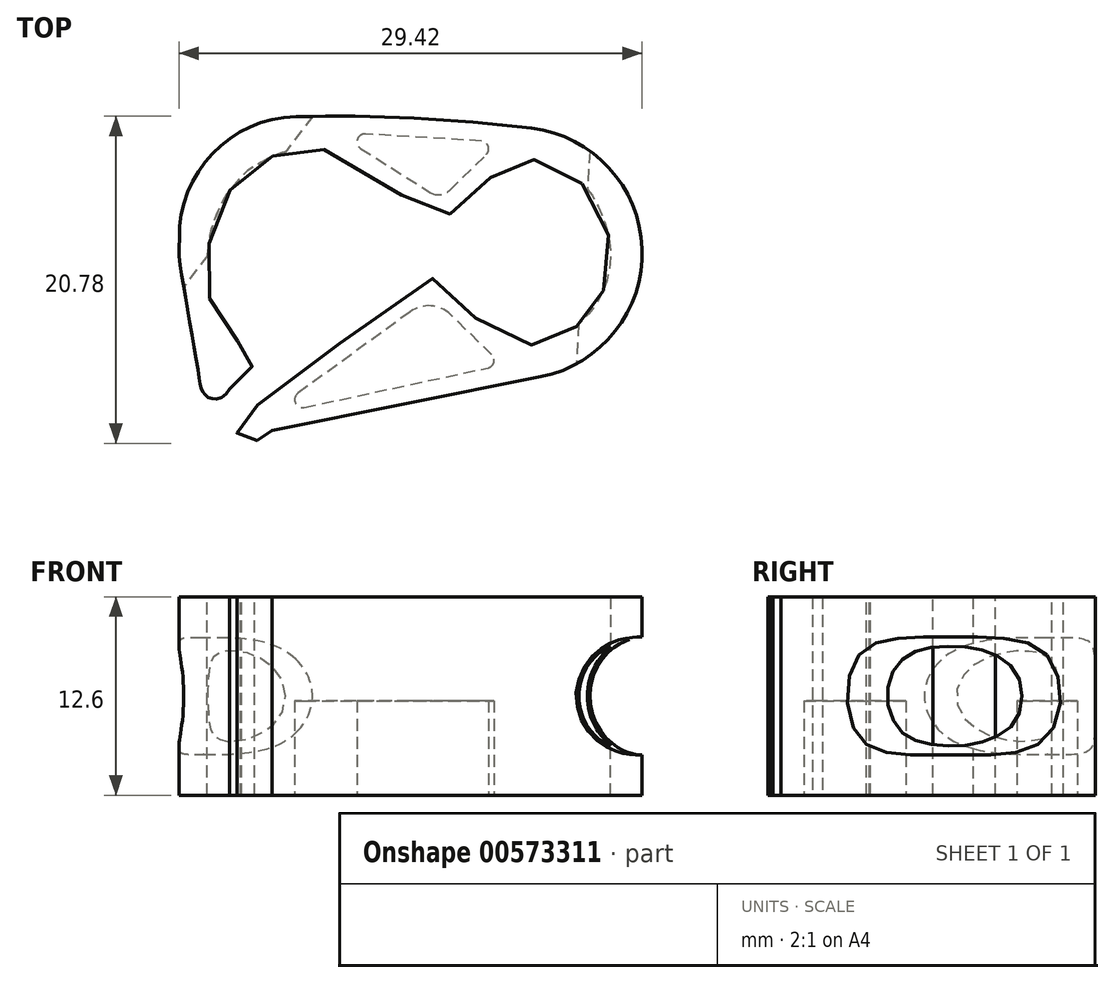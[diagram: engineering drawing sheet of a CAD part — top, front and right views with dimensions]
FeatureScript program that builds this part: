
annotation { "Feature Type Name" : "Feature", "Feature Type Description" : "" }
export const myFeature = defineFeature(function(context is Context, id is Id, definition is map)
    precondition{}
    {
        {
            var Q0;
            Q0=qCreatedBy(makeId("Top.planeOp"),FACE);
            var sketch = newSketch(context, id + "F0", { "sketchPlane" : qUnion([Q0])});
            skArc(sketch, "E0", {"start": v(11.96, -7.07) * mm, "mid": v(18.39, 1.08) * mm, "end": v(11.37, 8.72) * mm});
            skArc(sketch, "E1", {"start": v(-3.59, 9.45) * mm, "mid": v(-8.9, 7.12) * mm, "end": v(-11, 1.72) * mm});
            skArc(sketch, "E2", {"start": v(11.37, 8.72) * mm, "mid": v(3.9, 9.36) * mm, "end": v(-3.59, 9.45) * mm});
            skFitSpline(sketch, "E3", {"points": [v(-11, 1.72) * mm, v(-11, 0.44) * mm, v(-10.77, -1.18) * mm, v(-10.33, -3.66) * mm, v(-9.9, -6.13) * mm, v(-9.7, -7.38) * mm, v(-9.65, -7.7) * mm, v(-9.58, -7.94) * mm, v(-9.42, -8.15) * mm, v(-9.23, -8.35) * mm, v(-8.96, -8.46) * mm, v(-8.63, -8.5) * mm, v(-8.18, -8.3) * mm, v(-7.82, -7.86) * mm], "startDerivative": vector(-0.62, -12.7) * mm, "endDerivative": vector(4.68, 7.47) * mm});
            skLineSegment(sketch, "E4", {"start": v(11.96, -7.07) * mm, "end": v(-5.1, -10.48) * mm});
            skFitSpline(sketch, "E5", {"points": [v(-5.1, -10.48) * mm, v(-5.45, -10.95) * mm, v(-5.51, -11.02) * mm, v(-5.58, -11.03) * mm, v(-5.67, -11.01) * mm, v(-5.74, -11) * mm, v(-5.77, -10.98) * mm, v(-5.82, -11.05) * mm, v(-5.85, -11.1) * mm, v(-5.93, -11.15) * mm, v(-6.02, -11.14) * mm, v(-6.05, -11.12) * mm, v(-6.75, -11.28) * mm, v(-6.96, -11.3) * mm, v(-7.08, -11.26) * mm, v(-7.18, -11.17) * mm, v(-7.26, -11.04) * mm, v(-7.32, -10.93) * mm, v(-7.34, -10.79) * mm, v(-7.35, -10.64) * mm, v(-7.29, -10.48) * mm, v(-7.06, -10.26) * mm, v(-7.1, -10.05) * mm, v(-6.87, -9.77) * mm, v(-6.31, -9.21) * mm, v(-5.88, -8.63) * mm, v(-5.4, -8.14) * mm, v(-4.72, -7.68) * mm, v(4.34, -1.18) * mm, v(4.58, -0.98) * mm, v(4.82, -0.86) * mm, v(5.17, -0.83) * mm, v(5.56, -0.98) * mm, v(5.9, -1.3) * mm, v(6.49, -1.93) * mm, v(8.7, -4.2) * mm, v(9.71, -4.74) * mm, v(10.67, -4.97) * mm, v(11.62, -5.03) * mm, v(12.34, -4.91) * mm, v(13.23, -4.62) * mm, v(14.01, -4.1) * mm, v(14.42, -3.67) * mm, v(14.94, -3.13) * mm, v(15.4, -2.55) * mm, v(15.72, -2.02) * mm, v(16.03, -1.33) * mm, v(16.3, -0.28) * mm, v(16.38, 0.68) * mm, v(16.27, 1.83) * mm, v(15.86, 3.13) * mm, v(15.34, 4.24) * mm, v(14.78, 4.98) * mm, v(14, 5.72) * mm, v(13.41, 6.17) * mm, v(12.37, 6.61) * mm, v(11.34, 6.72) * mm, v(10.74, 6.69) * mm, v(10, 6.46) * mm, v(9.56, 6.24) * mm, v(8.52, 5.39) * mm, v(7.48, 4.54) * mm, v(6.74, 3.8) * mm, v(6.33, 3.35) * mm, v(5.89, 3.2) * mm, v(5.4, 3.17) * mm, v(4.52, 3.65) * mm, v(3.48, 4.24) * mm, v(-0.52, 6.9) * mm, v(-1.37, 7.2) * mm, v(-2, 7.43) * mm, v(-2.82, 7.43) * mm, v(-3.9, 7.28) * mm, v(-4.82, 7.06) * mm, v(-5.7, 6.61) * mm, v(-6.71, 5.98) * mm, v(-7.3, 5.35) * mm, v(-7.93, 4.61) * mm, v(-8.38, 3.8) * mm, v(-8.82, 2.76) * mm, v(-9.12, 1.42) * mm, v(-9.23, 0) * mm, v(-9.2, -0.5) * mm, v(-9.12, -1.62) * mm, v(-8.97, -2.36) * mm, v(-8.04, -3.17) * mm, v(-7.64, -3.62) * mm, v(-7.34, -4.7) * mm, v(-7.2, -4.88) * mm, v(-6.6, -4.8) * mm, v(-6.3, -5.1) * mm, v(-6.23, -5.73) * mm, v(-6.3, -6.28) * mm, v(-6.67, -6.73) * mm, v(-6.97, -7.17) * mm, v(-7.3, -7.36) * mm, v(-7.66, -7.5) * mm, v(-7.82, -7.6) * mm, v(-7.82, -7.86) * mm, v(-7.93, -8.02) * mm], "startDerivative": vector(-44.55, -59.06) * mm, "endDerivative": vector(-25.38, -25.79) * mm});
            skSolve(sketch);
        }
        {
            var Q0;
            Q0=makeQuery(id+"F0.imprint","IMPRINT",FACE,{"disambiguationData":[TD([[makeQuery(id+"F0.imprint","IMPRINT",EDGE,{"derivedFrom":sQuery(id+"F0.wireOp",EDGE,"E0")}),1.0]])]});
            extrude(context, id + "F1", {"entities" : qUnion([Q0]), "depth" : 12.6 * mm, "offsetDistance" : 25 * mm});
        }
        {
            var Q0;
            Q0=qCreatedBy(makeId("Top.planeOp"),FACE);
            var sketch = newSketch(context, id + "F2", { "sketchPlane" : qUnion([Q0])});
            skLineSegment(sketch, "E6", {"start": v(8.18, 7.9) * mm, "end": v(0.8, 8.35) * mm});
            skLineSegment(sketch, "E7", {"start": v(0.5, 7.43) * mm, "end": v(4.92, 4.64) * mm});
            skLineSegment(sketch, "E8", {"start": v(6.15, 4.77) * mm, "end": v(8.5, 7.05) * mm});
            skPoint(sketch, "E9.visualSharp", {"position": v(-1.13, 8.47) * mm});
            skArc(sketch, "E9.filletArc", {"start": v(0.8, 8.35) * mm, "mid": v(0.3, 8) * mm, "end": v(0.5, 7.43) * mm});
            skPoint(sketch, "E10.visualSharp", {"position": v(9.3, 7.84) * mm});
            skArc(sketch, "E10.filletArc", {"start": v(8.5, 7.05) * mm, "mid": v(8.62, 7.58) * mm, "end": v(8.18, 7.9) * mm});
            skPoint(sketch, "E11.visualSharp", {"position": v(5.59, 4.22) * mm});
            skArc(sketch, "E11.filletArc", {"start": v(4.92, 4.64) * mm, "mid": v(5.56, 4.5) * mm, "end": v(6.15, 4.77) * mm});
            skLineSegment(sketch, "E12", {"start": v(3.66, -2.94) * mm, "end": v(-3.47, -8.12) * mm});
            skLineSegment(sketch, "E13", {"start": v(-3.07, -9.01) * mm, "end": v(8.6, -6.5) * mm});
            skLineSegment(sketch, "E14", {"start": v(8.84, -5.66) * mm, "end": v(6.23, -3.12) * mm});
            skArc(sketch, "E15.filletArc", {"start": v(-3.47, -8.12) * mm, "mid": v(-3.64, -8.73) * mm, "end": v(-3.07, -9.01) * mm});
            skPoint(sketch, "E16.visualSharp", {"position": v(5.02, -1.95) * mm});
            skArc(sketch, "E16.filletArc", {"start": v(6.23, -3.12) * mm, "mid": v(4.98, -2.56) * mm, "end": v(3.66, -2.94) * mm});
            skPoint(sketch, "E17.visualSharp", {"position": v(9.5, -6.3) * mm});
            skArc(sketch, "E17.filletArc", {"start": v(8.6, -6.5) * mm, "mid": v(8.97, -6.16) * mm, "end": v(8.84, -5.66) * mm});
            skSolve(sketch);
        }
        {
            var Q0;
            Q0=makeQuery(id+"F2.imprint","IMPRINT",FACE,{"disambiguationData":[TD([[makeQuery(id+"F2.imprint","IMPRINT",EDGE,{"derivedFrom":sQuery(id+"F2.wireOp",EDGE,"E6")}),1.0]])]});
            var Q1;
            Q1=makeQuery(id+"F2.imprint","IMPRINT",FACE,{"disambiguationData":[TD([[makeQuery(id+"F2.imprint","IMPRINT",EDGE,{"derivedFrom":sQuery(id+"F2.wireOp",EDGE,"E12")}),1.0]])]});
            extrude(context, id + "F3", {"entities" : qUnion([Q0, Q1]), "operationType" : NewBodyOperationType.REMOVE, "depth" : 6 * mm, "offsetDistance" : 25 * mm});
        }
        {
            var Q0;
            Q0=makeQuery(id+"F1.opExtrude","CAP_FACE",FACE,{"disambiguationData":[OSD([sQuery(id+"F0.wireOp",EDGE,"E0"),sQuery(id+"F0.wireOp",EDGE,"E1"),sQuery(id+"F0.wireOp",EDGE,"E2"),sQuery(id+"F0.wireOp",EDGE,"E3"),sQuery(id+"F0.wireOp",EDGE,"E4"),sQuery(id+"F0.wireOp",EDGE,"E5")])],"isStart":false});
            var Q1;
            Q1=makeQuery(id+"F1.opExtrude","CAP_FACE",FACE,{"disambiguationData":[OSD([sQuery(id+"F0.wireOp",EDGE,"E0"),sQuery(id+"F0.wireOp",EDGE,"E1"),sQuery(id+"F0.wireOp",EDGE,"E2"),sQuery(id+"F0.wireOp",EDGE,"E3"),sQuery(id+"F0.wireOp",EDGE,"E4"),sQuery(id+"F0.wireOp",EDGE,"E5")])],"isStart":true});
            cPlane(context, id + "F4", {"entities" : qUnion([Q0, Q1]), "cplaneType" : CPlaneType.MID_PLANE, "offset" : 25 * mm, "width" : 150 * mm, "height" : 150 * mm});
        }
        {
            var Q0;
            Q0=makeQuery(id+"F1.opExtrude","SWEPT_EDGE",EDGE,{"disambiguationData":[OSD([sQuery(id+"F0.wireOp",EDGE,"E4"),sQuery(id+"F0.wireOp",EDGE,"E5")])]});
            cPlane(context, id + "F5", {"entities" : qUnion([Q0]), "cplaneType" : CPlaneType.LINE_ANGLE, "offset" : 25 * mm, "angle" : 53 * degree, "oppositeDirection" : true, "width" : 150 * mm, "height" : 150 * mm});
        }
        {
            var Q0;
            Q0=qCreatedBy(id+"F5.planeOp",FACE);
            var sketch = newSketch(context, id + "F6", { "sketchPlane" : qUnion([Q0])});
            skLineSegment(sketch, "E18.0.0", {"start": v(2.23, 0) * mm, "end": v(13.8, 0) * mm});
            skLineSegment(sketch, "E18.0.1", {"start": v(13.8, 0) * mm, "end": v(13.8, 12.6) * mm});
            skLineSegment(sketch, "E18.0.2", {"start": v(13.8, 12.6) * mm, "end": v(2.23, 12.6) * mm});
            skLineSegment(sketch, "E18.0.3", {"start": v(2.23, 12.6) * mm, "end": v(2.23, 0) * mm});
            skCircle(sketch, "E19", {"center": v(-11.44, 6.3) * mm, "radius": 3.7 * mm});
            skPoint(sketch, "E20", {"position": v(2.23, 6.3) * mm});
            skLineSegment(sketch, "E21", {"start": v(-11.44, 2.6) * mm, "end": v(-11.44, 10) * mm});
            skPoint(sketch, "E22.orphan", {"position": v(-11.44, 12.6) * mm});
            skPoint(sketch, "E23.orphan", {"position": v(-11.44, 0) * mm});
            skSolve(sketch);
        }
        {
            var Q0;
            {var subQ0=sQuery(id+"F6.wireOp",EDGE,"E21");Q0=makeQuery(id+"F6.imprint","IMPRINT",FACE,{"disambiguationData":[TD([[makeQuery(id+"F6.imprint","IMPRINT",EDGE,{"derivedFrom":subQ0}),1.0]])]});}
            var Q1;
            {var subQ0=sQuery(id+"F6.wireOp",EDGE,"E21");Q1=makeQuery(id+"F6.imprint","IMPRINT",FACE,{"disambiguationData":[TD([[makeQuery(id+"F6.imprint","IMPRINT",EDGE,{"derivedFrom":subQ0}),-1.0]])]});}
            extrude(context, id + "F7", {"entities" : qUnion([Q0, Q1]), "operationType" : NewBodyOperationType.REMOVE, "endBound" : BoundingType.THROUGH_ALL, "oppositeDirection" : true, "depth" : 25 * mm, "offsetDistance" : 25 * mm});
        }
        {
            var Q0;
            Q0=makeQuery(id+"F1.opExtrude","SWEPT_EDGE",EDGE,{"disambiguationData":[OSD([sQuery(id+"F0.wireOp",EDGE,"E0"),sQuery(id+"F0.wireOp",EDGE,"E4")])]});
            var Q1;
            Q1=makeQuery(id+"F1.opExtrude","SWEPT_FACE",FACE,{"disambiguationData":[OSD([sQuery(id+"F0.wireOp",EDGE,"E4")])]});
            cPlane(context, id + "F8", {"entities" : qUnion([Q0, Q1]), "cplaneType" : CPlaneType.LINE_ANGLE, "offset" : 25 * mm, "angle" : 15 * degree, "width" : 150 * mm, "height" : 150 * mm});
        }
        {
            var Q0;
            Q0=qCreatedBy(id+"F8.planeOp",FACE);
            var sketch = newSketch(context, id + "F9", { "sketchPlane" : qUnion([Q0])});
            skLineSegment(sketch, "E24.0", {"start": v(4.42, 12.6) * mm, "end": v(4.42, 0) * mm});
            skCircle(sketch, "E25", {"center": v(-18.32, 6.3) * mm, "radius": 3.75 * mm});
            skPoint(sketch, "E26", {"position": v(4.42, 6.3) * mm});
            skLineSegment(sketch, "E27", {"start": v(-18.32, 0) * mm, "end": v(-18.32, 12.6) * mm});
            skSolve(sketch);
        }
        {
            var Q0;
            {var subQ0=sQuery(id+"F9.wireOp",EDGE,"E27");var subQ1=sQuery(id+"F9.wireOp",EDGE,"E25");var subQ2=makeQuery(id+"F9.imprint","INTERSECT",VERTEX,{"disambiguationData":[OD(0.0)],"derivedFrom":[subQ1,subQ0]});Q0=makeQuery(id+"F9.imprint","IMPRINT",FACE,{"disambiguationData":[TD([[makeQuery(id+"F9.imprint","IMPRINT",EDGE,{"disambiguationData":[TD([[subQ2,1.0]])],"derivedFrom":subQ1}),1.0]])]});}
            var Q1;
            {var subQ0=sQuery(id+"F9.wireOp",EDGE,"E27");var subQ1=sQuery(id+"F9.wireOp",EDGE,"E25");var subQ2=makeQuery(id+"F9.imprint","INTERSECT",VERTEX,{"disambiguationData":[OD(0.0)],"derivedFrom":[subQ1,subQ0]});Q1=makeQuery(id+"F9.imprint","IMPRINT",FACE,{"disambiguationData":[TD([[makeQuery(id+"F9.imprint","IMPRINT",EDGE,{"disambiguationData":[TD([[subQ2,-1.0]])],"derivedFrom":subQ1}),1.0]])]});}
            extrude(context, id + "F10", {"entities" : qUnion([Q0, Q1]), "operationType" : NewBodyOperationType.REMOVE, "endBound" : BoundingType.THROUGH_ALL, "depth" : 25 * mm, "offsetDistance" : 25 * mm});
        }
    });
